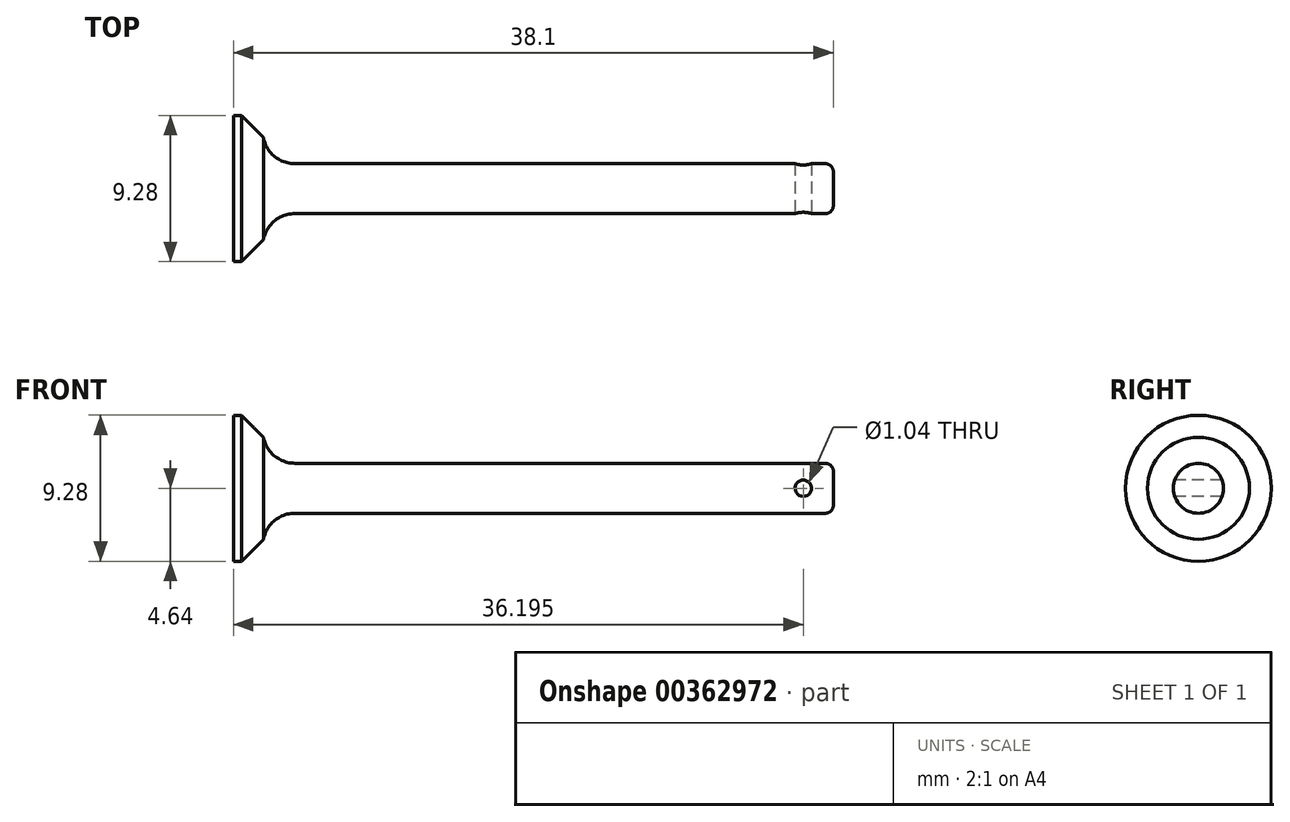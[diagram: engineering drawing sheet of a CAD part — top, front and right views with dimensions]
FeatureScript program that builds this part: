
annotation { "Feature Type Name" : "Feature", "Feature Type Description" : "" }
export const myFeature = defineFeature(function(context is Context, id is Id, definition is map)
    precondition{}
    {
        {
            var Q0;
            Q0=qCreatedBy(makeId("Front.planeOp"),FACE);
            var sketch = newSketch(context, id + "F0", { "sketchPlane" : qUnion([Q0])});
            skLineSegment(sketch, "E0", {"start": v(0, 0) * mm, "end": v(38.1, 0) * mm});
            skLineSegment(sketch, "E1", {"start": v(38.1, 0) * mm, "end": v(38.1, 1.59) * mm});
            skLineSegment(sketch, "E2", {"start": v(38.1, 1.59) * mm, "end": v(1.9, 1.59) * mm});
            skLineSegment(sketch, "E3", {"start": v(0, 0) * mm, "end": v(0, 4.64) * mm});
            skLineSegment(sketch, "E4", {"start": v(0, 4.64) * mm, "end": v(0.5, 4.64) * mm});
            skLineSegment(sketch, "E5", {"start": v(0.5, 4.64) * mm, "end": v(1.9, 3.24) * mm});
            skLineSegment(sketch, "E6.0", {"start": v(1.9, 1.59) * mm, "end": v(1.9, 3.24) * mm});
            skSolve(sketch);
        }
        {
            var Q0;
            Q0=makeQuery(id+"F0.imprint","IMPRINT",FACE,{"disambiguationData":[TD([[makeQuery(id+"F0.imprint","IMPRINT",EDGE,{"derivedFrom":sQuery(id+"F0.wireOp",EDGE,"E0")}),1.0]])]});
            var Q1;
            Q1=sQuery(id+"F0.wireOp",EDGE,"E0");
            revolve(context, id + "F1", {"entities" : qUnion([Q0]), "axis" : qUnion([Q1]), "revolveType" : RevolveType.FULL});
        }
        {
            var Q0;
            Q0=makeQuery(id+"F1.opRevolve","SWEPT_EDGE",EDGE,{"disambiguationData":[OSD([sQuery(id+"F0.wireOp",EDGE,"E2"),sQuery(id+"F0.wireOp",EDGE,"E6.0")])]});
            fillet(context, id + "F2", {"entities" : qUnion([Q0]), "radius" : 2.03 * mm, "tangentPropagation" : true, "allowEdgeOverflow" : false});
        }
        {
            var Q0;
            Q0=makeQuery(id+"F1.opRevolve","SWEPT_EDGE",EDGE,{"disambiguationData":[OSD([sQuery(id+"F0.wireOp",EDGE,"E1"),sQuery(id+"F0.wireOp",EDGE,"E2")])]});
            fillet(context, id + "F3", {"entities" : qUnion([Q0]), "radius" : 0.5 * mm, "tangentPropagation" : true, "allowEdgeOverflow" : false});
        }
        {
            var Q0;
            Q0=qCreatedBy(makeId("Front.planeOp"),FACE);
            var sketch = newSketch(context, id + "F4", { "sketchPlane" : qUnion([Q0])});
            skCircle(sketch, "E7", {"center": v(36.2, 0) * mm, "radius": 0.52 * mm});
            skSolve(sketch);
        }
        {
            var Q0;
            Q0=qCreatedBy(makeId("Front.planeOp"),FACE);
            cPlane(context, id + "F5", {"entities" : qUnion([Q0]), "cplaneType" : CPlaneType.OFFSET, "offset" : 5.08 * mm, "width" : 152.4 * mm, "height" : 152.4 * mm});
        }
        {
            var Q0;
            Q0=qCreatedBy(id+"F5.planeOp",FACE);
            var sketch = newSketch(context, id + "F6", { "sketchPlane" : qUnion([Q0])});
            skCircle(sketch, "E8.0", {"center": v(36.2, 0) * mm, "radius": 0.52 * mm});
            skSolve(sketch);
        }
        {
            var Q0;
            Q0=makeQuery(id+"F6.imprint","IMPRINT",FACE,{"disambiguationData":[TD([[makeQuery(id+"F6.imprint","IMPRINT",EDGE,{"derivedFrom":sQuery(id+"F6.wireOp",EDGE,"E8.0")}),1.0]])]});
            extrude(context, id + "F7", {"entities" : qUnion([Q0]), "operationType" : NewBodyOperationType.REMOVE, "endBound" : BoundingType.THROUGH_ALL, "oppositeDirection" : true, "depth" : 25.4 * mm});
        }
    });
